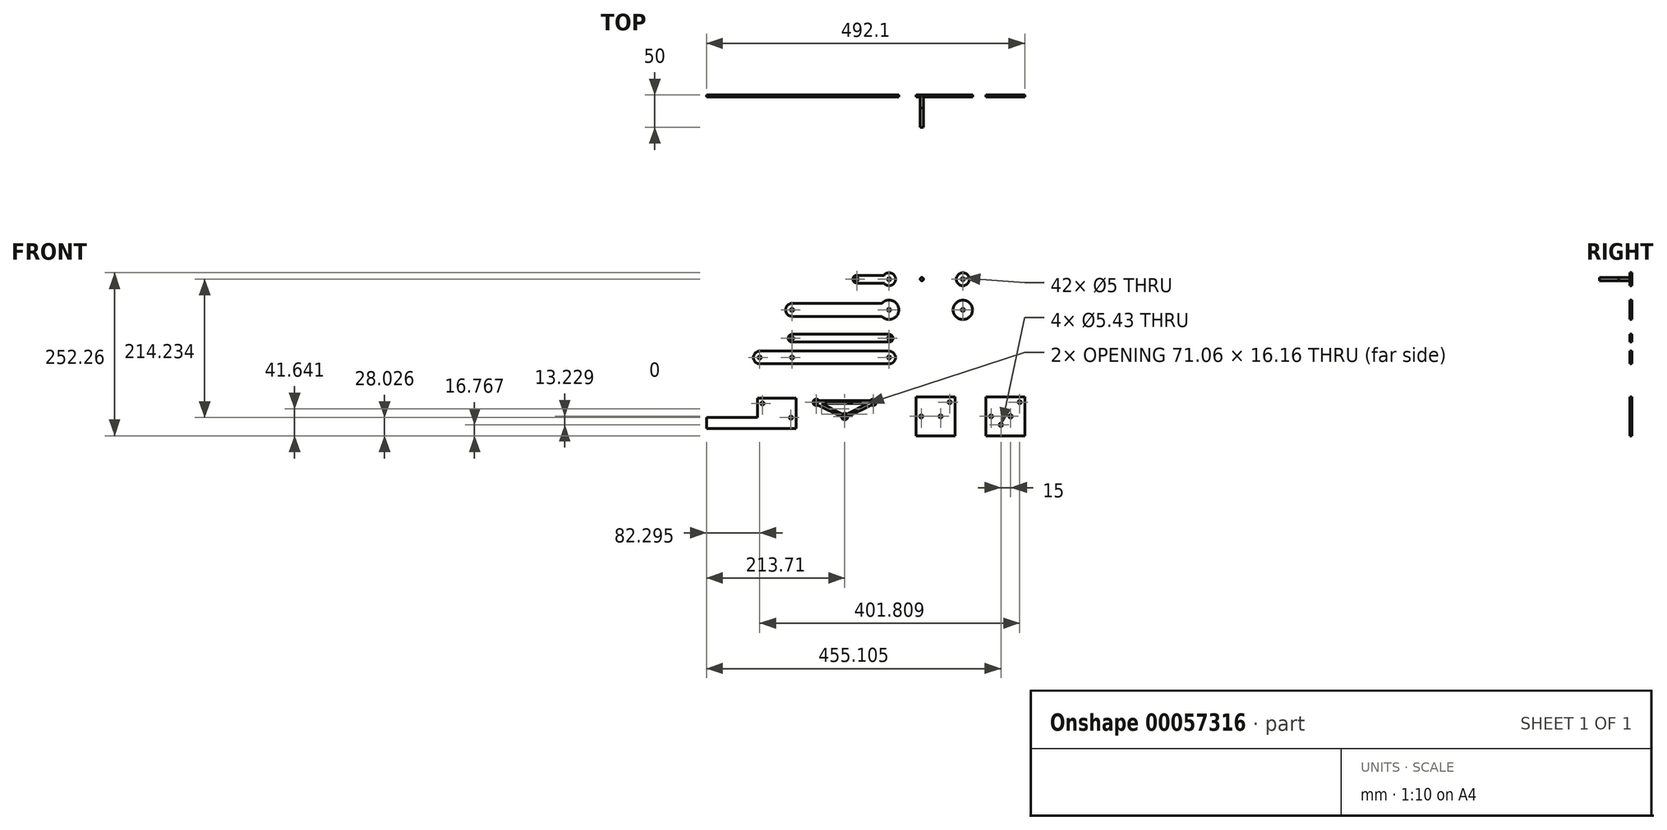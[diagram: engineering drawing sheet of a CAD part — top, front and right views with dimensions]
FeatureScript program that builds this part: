
annotation { "Feature Type Name" : "Feature", "Feature Type Description" : "" }
export const myFeature = defineFeature(function(context is Context, id is Id, definition is map)
    precondition{}
    {
        {
            var Q0;
            Q0=qCreatedBy(makeId("Front.planeOp"),FACE);
            var sketch = newSketch(context, id + "F0", { "sketchPlane" : qUnion([Q0])});
            skCircle(sketch, "E0", {"center": v(0, 0) * mm, "radius": 15 * mm});
            skArc(sketch, "E1", {"start": v(-122.04, 41.44) * mm, "mid": v(-104.04, 47.44) * mm, "end": v(-122.04, 53.44) * mm});
            skArc(sketch, "E2", {"start": v(-125.22, -10) * mm, "mid": v(-99.04, 0) * mm, "end": v(-125.22, 10) * mm});
            skCircle(sketch, "E3", {"center": v(0, 47.44) * mm, "radius": 10 * mm});
            skLineSegment(sketch, "E4.bottom", {"start": v(-122.04, 53.44) * mm, "end": v(-164.04, 53.44) * mm});
            skLineSegment(sketch, "E4.top", {"start": v(-122.04, 41.44) * mm, "end": v(-164.04, 41.44) * mm});
            skArc(sketch, "E5", {"start": v(-164.04, 53.44) * mm, "mid": v(-170.04, 47.44) * mm, "end": v(-164.04, 41.44) * mm});
            skLineSegment(sketch, "E6.bottom", {"start": v(-125.22, 10) * mm, "end": v(-264.04, 10) * mm});
            skLineSegment(sketch, "E6.top", {"start": v(-125.22, -10) * mm, "end": v(-264.04, -10) * mm});
            skPoint(sketch, "E7.orphan", {"position": v(-114.04, 41.44) * mm});
            skPoint(sketch, "E4.left.start.orphan", {"position": v(-114.04, 53.44) * mm});
            skPoint(sketch, "E8.orphan", {"position": v(-114.04, 10) * mm});
            skPoint(sketch, "E9.orphan", {"position": v(-114.04, -10) * mm});
            skArc(sketch, "E10", {"start": v(-264.04, 10) * mm, "mid": v(-274.04, 0) * mm, "end": v(-264.04, -10) * mm});
            skLineSegment(sketch, "E11.bottom", {"start": v(-114.04, -37.87) * mm, "end": v(-264.04, -37.87) * mm});
            skLineSegment(sketch, "E11.top", {"start": v(-114.04, -49.87) * mm, "end": v(-264.04, -49.87) * mm});
            skLineSegment(sketch, "E11.left", {"start": v(-114.04, -37.87) * mm, "end": v(-114.04, -49.87) * mm});
            skLineSegment(sketch, "E11.right", {"start": v(-264.04, -37.87) * mm, "end": v(-264.04, -49.87) * mm});
            skLineSegment(sketch, "E12", {"start": v(-164.04, 53.44) * mm, "end": v(-164.04, 41.44) * mm, "construction": true});
            skLineSegment(sketch, "E13", {"start": v(-264.04, 10) * mm, "end": v(-264.04, -10) * mm, "construction": true});
            skCircle(sketch, "E14", {"center": v(-264.04, -43.87) * mm, "radius": 6 * mm});
            skCircle(sketch, "E15", {"center": v(-114.04, -43.87) * mm, "radius": 6 * mm});
            skLineSegment(sketch, "E16.bottom", {"start": v(-114.04, -63.88) * mm, "end": v(-314.04, -63.88) * mm});
            skLineSegment(sketch, "E16.top", {"start": v(-114.04, -83.6) * mm, "end": v(-314.04, -83.6) * mm});
            skLineSegment(sketch, "E16.left", {"start": v(-114.04, -63.88) * mm, "end": v(-114.04, -83.6) * mm});
            skLineSegment(sketch, "E16.right", {"start": v(-314.04, -63.88) * mm, "end": v(-314.04, -83.6) * mm});
            skCircle(sketch, "E17", {"center": v(-314.04, -73.74) * mm, "radius": 9.86 * mm});
            skLineSegment(sketch, "E18", {"start": v(-314.04, -73.74) * mm, "end": v(-264.04, -73.74) * mm, "construction": true});
            skCircle(sketch, "E19", {"center": v(-264.04, -73.74) * mm, "radius": 9.86 * mm});
            skLineSegment(sketch, "E20", {"start": v(-164.04, 47.44) * mm, "end": v(-114.04, 47.44) * mm, "construction": true});
            skLineSegment(sketch, "E21", {"start": v(-264.04, -73.74) * mm, "end": v(-114.04, -73.74) * mm, "construction": true});
            skLineSegment(sketch, "E22", {"start": v(-114.04, 0) * mm, "end": v(-264.04, 0) * mm, "construction": true});
            skCircle(sketch, "E23", {"center": v(-114.04, -73.74) * mm, "radius": 9.86 * mm});
            skLineSegment(sketch, "E24.bottom", {"start": v(-72.32, -134.82) * mm, "end": v(-12.32, -134.82) * mm});
            skLineSegment(sketch, "E24.top", {"start": v(-72.32, -194.82) * mm, "end": v(-12.32, -194.82) * mm});
            skLineSegment(sketch, "E24.left", {"start": v(-72.32, -134.82) * mm, "end": v(-72.32, -194.82) * mm});
            skLineSegment(sketch, "E24.right", {"start": v(-12.32, -134.82) * mm, "end": v(-12.32, -194.82) * mm});
            skLineSegment(sketch, "E25.bottom", {"start": v(-72.32, -134.82) * mm, "end": v(-64.32, -134.82) * mm, "construction": true});
            skLineSegment(sketch, "E25.top", {"start": v(-72.32, -164.82) * mm, "end": v(-64.32, -164.82) * mm, "construction": true});
            skLineSegment(sketch, "E25.left", {"start": v(-72.32, -134.82) * mm, "end": v(-72.32, -164.82) * mm, "construction": true});
            skLineSegment(sketch, "E25.right", {"start": v(-64.32, -134.82) * mm, "end": v(-64.32, -164.82) * mm, "construction": true});
            skLineSegment(sketch, "E26.bottom", {"start": v(-72.32, -134.82) * mm, "end": v(-20.32, -134.82) * mm, "construction": true});
            skLineSegment(sketch, "E26.left", {"start": v(-72.32, -134.82) * mm, "end": v(-72.32, -149.82) * mm, "construction": true});
            skLineSegment(sketch, "E27.bottom", {"start": v(-257.77, -183.56) * mm, "end": v(-396.34, -183.56) * mm});
            skLineSegment(sketch, "E27.left", {"start": v(-257.77, -183.56) * mm, "end": v(-257.77, -163.85) * mm});
            skLineSegment(sketch, "E27.right", {"start": v(-396.34, -183.56) * mm, "end": v(-396.34, -166.73) * mm});
            skLineSegment(sketch, "E28.top", {"start": v(-257.77, -136.8) * mm, "end": v(-317.77, -136.8) * mm});
            skLineSegment(sketch, "E28.left", {"start": v(-257.77, -163.85) * mm, "end": v(-257.77, -136.8) * mm});
            skLineSegment(sketch, "E28.right", {"start": v(-317.77, -166.73) * mm, "end": v(-317.77, -136.8) * mm});
            skLineSegment(sketch, "E29.top", {"start": v(-72.32, -142.82) * mm, "end": v(-20.32, -142.82) * mm, "construction": true});
            skLineSegment(sketch, "E29.left", {"start": v(-72.32, -134.82) * mm, "end": v(-72.32, -142.82) * mm, "construction": true});
            skLineSegment(sketch, "E29.right", {"start": v(-20.32, -134.82) * mm, "end": v(-20.32, -142.82) * mm, "construction": true});
            skLineSegment(sketch, "E30.bottom", {"start": v(-257.77, -136.8) * mm, "end": v(-265.77, -136.8) * mm, "construction": true});
            skLineSegment(sketch, "E30.left", {"start": v(-257.77, -136.8) * mm, "end": v(-257.77, -166.8) * mm, "construction": true});
            skLineSegment(sketch, "E30.right", {"start": v(-265.77, -136.8) * mm, "end": v(-265.77, -166.8) * mm, "construction": true});
            skLineSegment(sketch, "E31.bottom", {"start": v(-257.77, -136.8) * mm, "end": v(-309.77, -136.8) * mm, "construction": true});
            skLineSegment(sketch, "E31.top", {"start": v(-257.77, -144.8) * mm, "end": v(-309.77, -144.8) * mm, "construction": true});
            skLineSegment(sketch, "E31.left", {"start": v(-257.77, -136.8) * mm, "end": v(-257.77, -144.8) * mm, "construction": true});
            skLineSegment(sketch, "E31.right", {"start": v(-309.77, -136.8) * mm, "end": v(-309.77, -144.8) * mm, "construction": true});
            skLineSegment(sketch, "E32.trimOffspring", {"start": v(-317.77, -166.73) * mm, "end": v(-396.34, -166.73) * mm});
            skLineSegment(sketch, "E33", {"start": v(-309.77, -144.8) * mm, "end": v(-265.77, -166.8) * mm, "construction": true});
            skLineSegment(sketch, "E34", {"start": v(-64.32, -164.82) * mm, "end": v(-20.32, -142.82) * mm, "construction": true});
            skLineSegment(sketch, "E35", {"start": v(-226.63, -143.1) * mm, "end": v(-182.63, -143.1) * mm, "construction": true});
            skLineSegment(sketch, "E36", {"start": v(-182.63, -143.1) * mm, "end": v(-138.63, -143.1) * mm, "construction": true});
            skLineSegment(sketch, "E37", {"start": v(-182.63, -143.1) * mm, "end": v(-182.63, -165.1) * mm, "construction": true});
            skLineSegment(sketch, "E38", {"start": v(-226.63, -143.1) * mm, "end": v(-182.63, -165.1) * mm, "construction": true});
            skLineSegment(sketch, "E39", {"start": v(-182.63, -165.1) * mm, "end": v(-138.63, -143.1) * mm, "construction": true});
            skCircle(sketch, "E40", {"center": v(-226.63, -143.1) * mm, "radius": 2.5 * mm});
            skCircle(sketch, "E41", {"center": v(-138.63, -143.1) * mm, "radius": 2.5 * mm});
            skCircle(sketch, "E42", {"center": v(-182.63, -165.1) * mm, "radius": 2.5 * mm});
            skCircle(sketch, "E43", {"center": v(-20.32, -142.82) * mm, "radius": 2.5 * mm});
            skCircle(sketch, "E44", {"center": v(-64.32, -164.82) * mm, "radius": 2.5 * mm});
            skCircle(sketch, "E45", {"center": v(-265.77, -166.8) * mm, "radius": 2.5 * mm});
            skCircle(sketch, "E46", {"center": v(-309.77, -144.8) * mm, "radius": 2.5 * mm});
            skCircle(sketch, "E47", {"center": v(-314.04, -73.74) * mm, "radius": 2.5 * mm});
            skCircle(sketch, "E48", {"center": v(-264.04, -73.74) * mm, "radius": 2.5 * mm});
            skCircle(sketch, "E49", {"center": v(-114.04, -73.74) * mm, "radius": 2.5 * mm});
            skCircle(sketch, "E50", {"center": v(-264.04, -43.87) * mm, "radius": 2.5 * mm});
            skCircle(sketch, "E51", {"center": v(-114.04, -43.87) * mm, "radius": 2.5 * mm});
            skCircle(sketch, "E52", {"center": v(-264.04, 0) * mm, "radius": 2.5 * mm});
            skCircle(sketch, "E53", {"center": v(-114.04, 0) * mm, "radius": 2.5 * mm});
            skCircle(sketch, "E54", {"center": v(-114.04, 47.44) * mm, "radius": 2.5 * mm});
            skCircle(sketch, "E55", {"center": v(-164.04, 47.44) * mm, "radius": 2.5 * mm});
            skCircle(sketch, "E56", {"center": v(0, 47.44) * mm, "radius": 2.5 * mm});
            skCircle(sketch, "E57", {"center": v(0, 0) * mm, "radius": 2.5 * mm});
            skArc(sketch, "E58", {"start": v(-222.3, -140.6) * mm, "mid": v(-231.5, -141.95) * mm, "end": v(-223.88, -147.27) * mm});
            skArc(sketch, "E59", {"start": v(-187.62, -165.4) * mm, "mid": v(-182.63, -170.1) * mm, "end": v(-177.64, -165.4) * mm});
            skArc(sketch, "E60", {"start": v(-141.38, -147.27) * mm, "mid": v(-133.76, -141.95) * mm, "end": v(-142.96, -140.6) * mm});
            skLineSegment(sketch, "E61.0", {"start": v(-182.63, -140.6) * mm, "end": v(-142.96, -140.6) * mm});
            skLineSegment(sketch, "E61.1", {"start": v(-222.3, -140.6) * mm, "end": v(-182.63, -140.6) * mm});
            skLineSegment(sketch, "E62.1", {"start": v(-223.88, -147.27) * mm, "end": v(-187.62, -165.4) * mm});
            skLineSegment(sketch, "E63.0", {"start": v(-218.16, -145.1) * mm, "end": v(-185.83, -161.26) * mm});
            skLineSegment(sketch, "E63.1", {"start": v(-218.16, -145.1) * mm, "end": v(-182.63, -145.1) * mm});
            skLineSegment(sketch, "E63.2", {"start": v(-182.63, -145.1) * mm, "end": v(-147.1, -145.1) * mm});
            skLineSegment(sketch, "E64.trimOffspring", {"start": v(-179.43, -161.26) * mm, "end": v(-147.1, -145.1) * mm});
            skLineSegment(sketch, "E65.trimOffspring", {"start": v(-177.64, -165.4) * mm, "end": v(-141.38, -147.27) * mm});
            skArc(sketch, "E66.trimOffspring", {"start": v(-179.43, -161.26) * mm, "mid": v(-182.63, -160.1) * mm, "end": v(-185.83, -161.26) * mm});
            skLineSegment(sketch, "E67", {"start": v(-64.32, -164.82) * mm, "end": v(-34.32, -164.82) * mm, "construction": true});
            skCircle(sketch, "E68", {"center": v(-34.32, -164.82) * mm, "radius": 2.5 * mm});
            skLineSegment(sketch, "E69.1.0.0", {"start": v(43.76, -134.82) * mm, "end": v(43.76, -164.82) * mm, "construction": true});
            skLineSegment(sketch, "E69.1.0.1", {"start": v(43.76, -164.82) * mm, "end": v(73.76, -164.82) * mm, "construction": true});
            skLineSegment(sketch, "E69.1.0.2", {"start": v(35.76, -134.82) * mm, "end": v(95.76, -134.82) * mm});
            skLineSegment(sketch, "E69.1.0.3", {"start": v(95.76, -134.82) * mm, "end": v(95.76, -194.82) * mm});
            skLineSegment(sketch, "E69.1.0.4", {"start": v(35.76, -164.82) * mm, "end": v(43.76, -164.82) * mm, "construction": true});
            skLineSegment(sketch, "E69.1.0.5", {"start": v(43.76, -164.82) * mm, "end": v(87.76, -142.82) * mm, "construction": true});
            skCircle(sketch, "E69.1.0.6", {"center": v(87.76, -142.82) * mm, "radius": 2.5 * mm});
            skCircle(sketch, "E69.1.0.7", {"center": v(73.76, -164.82) * mm, "radius": 2.72 * mm});
            skLineSegment(sketch, "E69.1.0.8", {"start": v(35.76, -134.82) * mm, "end": v(35.76, -194.82) * mm});
            skLineSegment(sketch, "E69.1.0.9", {"start": v(35.76, -194.82) * mm, "end": v(95.76, -194.82) * mm});
            skLineSegment(sketch, "E69.1.0.10", {"start": v(35.76, -142.82) * mm, "end": v(87.76, -142.82) * mm, "construction": true});
            skLineSegment(sketch, "E69.1.0.11", {"start": v(35.76, -134.82) * mm, "end": v(43.76, -134.82) * mm, "construction": true});
            skLineSegment(sketch, "E69.1.0.12", {"start": v(35.76, -134.82) * mm, "end": v(35.76, -164.82) * mm, "construction": true});
            skLineSegment(sketch, "E69.1.0.13", {"start": v(35.76, -134.82) * mm, "end": v(87.76, -134.82) * mm, "construction": true});
            skLineSegment(sketch, "E69.1.0.14", {"start": v(35.76, -134.82) * mm, "end": v(87.76, -134.82) * mm, "construction": true});
            skLineSegment(sketch, "E69.1.0.15", {"start": v(35.76, -134.82) * mm, "end": v(35.76, -149.82) * mm, "construction": true});
            skLineSegment(sketch, "E69.1.0.16", {"start": v(87.76, -134.82) * mm, "end": v(87.76, -142.82) * mm, "construction": true});
            skLineSegment(sketch, "E69.1.0.17", {"start": v(35.76, -134.82) * mm, "end": v(35.76, -142.82) * mm, "construction": true});
            skCircle(sketch, "E69.1.0.18", {"center": v(43.76, -164.82) * mm, "radius": 2.5 * mm});
            skLineSegment(sketch, "E70", {"start": v(43.76, -164.82) * mm, "end": v(58.76, -178.05) * mm, "construction": true});
            skLineSegment(sketch, "E71", {"start": v(58.76, -178.05) * mm, "end": v(73.76, -164.82) * mm, "construction": true});
            skCircle(sketch, "E72", {"center": v(58.76, -178.05) * mm, "radius": 2.72 * mm});
            skCircle(sketch, "E73", {"center": v(-381.55, 5.43) * mm, "radius": 2.5 * mm});
            skSolve(sketch);
        }
        {
            var Q0;
            Q0=makeQuery(id+"F0.imprint","IMPRINT",FACE,{"disambiguationData":[TD([[makeQuery(id+"F0.imprint","IMPRINT",EDGE,{"derivedFrom":sQuery(id+"F0.wireOp",EDGE,"E0")}),1.0]])]});
            var Q1;
            Q1=makeQuery(id+"F0.imprint","IMPRINT",FACE,{"disambiguationData":[TD([[makeQuery(id+"F0.imprint","IMPRINT",EDGE,{"derivedFrom":sQuery(id+"F0.wireOp",EDGE,"E3")}),1.0]])]});
            var Q2;
            Q2=makeQuery(id+"F0.imprint","IMPRINT",FACE,{"disambiguationData":[TD([[makeQuery(id+"F0.imprint","IMPRINT",EDGE,{"derivedFrom":sQuery(id+"F0.wireOp",EDGE,"E1")}),1.0]])]});
            var Q3;
            Q3=makeQuery(id+"F0.imprint","IMPRINT",FACE,{"disambiguationData":[TD([[makeQuery(id+"F0.imprint","IMPRINT",EDGE,{"derivedFrom":sQuery(id+"F0.wireOp",EDGE,"E2")}),1.0]])]});
            var Q4;
            {var subQ0=sQuery(id+"F0.wireOp",EDGE,"E11.bottom");Q4=makeQuery(id+"F0.imprint","IMPRINT",FACE,{"disambiguationData":[TD([[makeQuery(id+"F0.imprint","IMPRINT",EDGE,{"derivedFrom":subQ0}),1.0]])]});}
            var Q5;
            {var subQ1=sQuery(id+"F0.wireOp",EDGE,"E11.left");var subQ3=sQuery(id+"F0.wireOp",EDGE,"E51");var subQ4=makeQuery(id+"F0.imprint","INTERSECT",VERTEX,{"disambiguationData":[OD(0.0)],"derivedFrom":[subQ1,subQ3]});Q5=makeQuery(id+"F0.imprint","IMPRINT",FACE,{"disambiguationData":[TD([[makeQuery(id+"F0.imprint","IMPRINT",EDGE,{"disambiguationData":[TD([[subQ4,1.0]])],"derivedFrom":subQ3}),-1.0]])]});}
            var Q6;
            {var subQ1=sQuery(id+"F0.wireOp",EDGE,"E11.right");var subQ3=sQuery(id+"F0.wireOp",EDGE,"E50");var subQ4=makeQuery(id+"F0.imprint","INTERSECT",VERTEX,{"disambiguationData":[OD(0.0)],"derivedFrom":[subQ1,subQ3]});Q6=makeQuery(id+"F0.imprint","IMPRINT",FACE,{"disambiguationData":[TD([[makeQuery(id+"F0.imprint","IMPRINT",EDGE,{"disambiguationData":[TD([[subQ4,-1.0]])],"derivedFrom":subQ3}),-1.0]])]});}
            var Q7;
            {var subQ2=sQuery(id+"F0.wireOp",EDGE,"E16.bottom");var subQ4=sQuery(id+"F0.wireOp",EDGE,"E19");var subQ5=makeQuery(id+"F0.imprint","INTERSECT",VERTEX,{"derivedFrom":[subQ2,subQ4]});Q7=makeQuery(id+"F0.imprint","IMPRINT",FACE,{"disambiguationData":[TD([[makeQuery(id+"F0.imprint","IMPRINT",EDGE,{"disambiguationData":[TD([[subQ5,1.0]])],"derivedFrom":subQ4}),-1.0]])]});}
            var Q8;
            {var subQ2=sQuery(id+"F0.wireOp",EDGE,"E16.bottom");var subQ4=sQuery(id+"F0.wireOp",EDGE,"E19");var subQ5=makeQuery(id+"F0.imprint","INTERSECT",VERTEX,{"derivedFrom":[subQ2,subQ4]});Q8=makeQuery(id+"F0.imprint","IMPRINT",FACE,{"disambiguationData":[TD([[makeQuery(id+"F0.imprint","IMPRINT",EDGE,{"disambiguationData":[TD([[subQ5,-1.0]])],"derivedFrom":subQ4}),-1.0]])]});}
            var Q9;
            {var subQ1=sQuery(id+"F0.wireOp",EDGE,"E16.left");var subQ3=sQuery(id+"F0.wireOp",EDGE,"E49");var subQ4=makeQuery(id+"F0.imprint","INTERSECT",VERTEX,{"disambiguationData":[OD(0.0)],"derivedFrom":[subQ1,subQ3]});Q9=makeQuery(id+"F0.imprint","IMPRINT",FACE,{"disambiguationData":[TD([[makeQuery(id+"F0.imprint","IMPRINT",EDGE,{"disambiguationData":[TD([[subQ4,1.0]])],"derivedFrom":subQ3}),-1.0]])]});}
            var Q10;
            {var subQ1=sQuery(id+"F0.wireOp",EDGE,"E16.right");var subQ3=sQuery(id+"F0.wireOp",EDGE,"E47");var subQ4=makeQuery(id+"F0.imprint","INTERSECT",VERTEX,{"disambiguationData":[OD(0.0)],"derivedFrom":[subQ1,subQ3]});Q10=makeQuery(id+"F0.imprint","IMPRINT",FACE,{"disambiguationData":[TD([[makeQuery(id+"F0.imprint","IMPRINT",EDGE,{"disambiguationData":[TD([[subQ4,-1.0]])],"derivedFrom":subQ3}),-1.0]])]});}
            var Q11;
            Q11=makeQuery(id+"F0.imprint","IMPRINT",FACE,{"disambiguationData":[TD([[makeQuery(id+"F0.imprint","IMPRINT",EDGE,{"derivedFrom":sQuery(id+"F0.wireOp",EDGE,"E27.bottom")}),-1.0]])]});
            var Q12;
            {var subQ1=sQuery(id+"F0.wireOp",EDGE,"E11.left");var subQ3=sQuery(id+"F0.wireOp",EDGE,"E51");var subQ4=makeQuery(id+"F0.imprint","INTERSECT",VERTEX,{"disambiguationData":[OD(0.0)],"derivedFrom":[subQ1,subQ3]});Q12=makeQuery(id+"F0.imprint","IMPRINT",FACE,{"disambiguationData":[TD([[makeQuery(id+"F0.imprint","IMPRINT",EDGE,{"disambiguationData":[TD([[subQ4,-1.0]])],"derivedFrom":subQ3}),-1.0]])]});}
            var Q13;
            {var subQ1=sQuery(id+"F0.wireOp",EDGE,"E11.right");var subQ3=sQuery(id+"F0.wireOp",EDGE,"E50");var subQ4=makeQuery(id+"F0.imprint","INTERSECT",VERTEX,{"disambiguationData":[OD(0.0)],"derivedFrom":[subQ1,subQ3]});Q13=makeQuery(id+"F0.imprint","IMPRINT",FACE,{"disambiguationData":[TD([[makeQuery(id+"F0.imprint","IMPRINT",EDGE,{"disambiguationData":[TD([[subQ4,1.0]])],"derivedFrom":subQ3}),-1.0]])]});}
            var Q14;
            {var subQ1=sQuery(id+"F0.wireOp",EDGE,"E16.left");var subQ3=sQuery(id+"F0.wireOp",EDGE,"E49");var subQ4=makeQuery(id+"F0.imprint","INTERSECT",VERTEX,{"disambiguationData":[OD(0.0)],"derivedFrom":[subQ1,subQ3]});Q14=makeQuery(id+"F0.imprint","IMPRINT",FACE,{"disambiguationData":[TD([[makeQuery(id+"F0.imprint","IMPRINT",EDGE,{"disambiguationData":[TD([[subQ4,-1.0]])],"derivedFrom":subQ3}),-1.0]])]});}
            var Q15;
            {var subQ1=sQuery(id+"F0.wireOp",EDGE,"E16.right");var subQ3=sQuery(id+"F0.wireOp",EDGE,"E47");var subQ4=makeQuery(id+"F0.imprint","INTERSECT",VERTEX,{"disambiguationData":[OD(0.0)],"derivedFrom":[subQ1,subQ3]});Q15=makeQuery(id+"F0.imprint","IMPRINT",FACE,{"disambiguationData":[TD([[makeQuery(id+"F0.imprint","IMPRINT",EDGE,{"disambiguationData":[TD([[subQ4,1.0]])],"derivedFrom":subQ3}),-1.0]])]});}
            var Q16;
            Q16=makeQuery(id+"F0.imprint","IMPRINT",FACE,{"disambiguationData":[TD([[makeQuery(id+"F0.imprint","IMPRINT",EDGE,{"derivedFrom":sQuery(id+"F0.wireOp",EDGE,"E48")}),-1.0]])]});
            var Q17;
            Q17=makeQuery(id+"F0.imprint","IMPRINT",FACE,{"disambiguationData":[TD([[makeQuery(id+"F0.imprint","IMPRINT",EDGE,{"derivedFrom":sQuery(id+"F0.wireOp",EDGE,"E24.bottom")}),-1.0]])]});
            var Q18;
            Q18=makeQuery(id+"F0.imprint","IMPRINT",FACE,{"disambiguationData":[TD([[makeQuery(id+"F0.imprint","IMPRINT",EDGE,{"derivedFrom":sQuery(id+"F0.wireOp",EDGE,"E40")}),-1.0]])]});
            var Q19;
            Q19=makeQuery(id+"F0.imprint","IMPRINT",FACE,{"disambiguationData":[TD([[makeQuery(id+"F0.imprint","IMPRINT",EDGE,{"derivedFrom":sQuery(id+"F0.wireOp",EDGE,"E69.1.0.2")}),-1.0]])]});
            extrude(context, id + "F1", {"entities" : qUnion([Q0, Q1, Q2, Q3, Q4, Q5, Q6, Q7, Q8, Q9, Q10, Q11, Q12, Q13, Q14, Q15, Q16, Q17, Q18, Q19]), "depth" : 3 * mm});
        }
        {
            var Q0;
            Q0=qCreatedBy(makeId("Front.planeOp"),FACE);
            var sketch = newSketch(context, id + "F2", { "sketchPlane" : qUnion([Q0])});
            skCircle(sketch, "E74", {"center": v(-63.37, 47.55) * mm, "radius": 2.5 * mm});
            skSolve(sketch);
        }
        {
            var Q0;
            Q0 = qSketchRegion(id + "F2", true);
            extrude(context, id + "F3", {"entities" : qUnion([Q0]), "depth" : 50 * mm});
        }
        {
            var Q0;
            Q0 = qSketchRegion(id + "F2", true);
            extrude(context, id + "F4", {"entities" : qUnion([Q0]), "depth" : 20 * mm});
        }
    });
